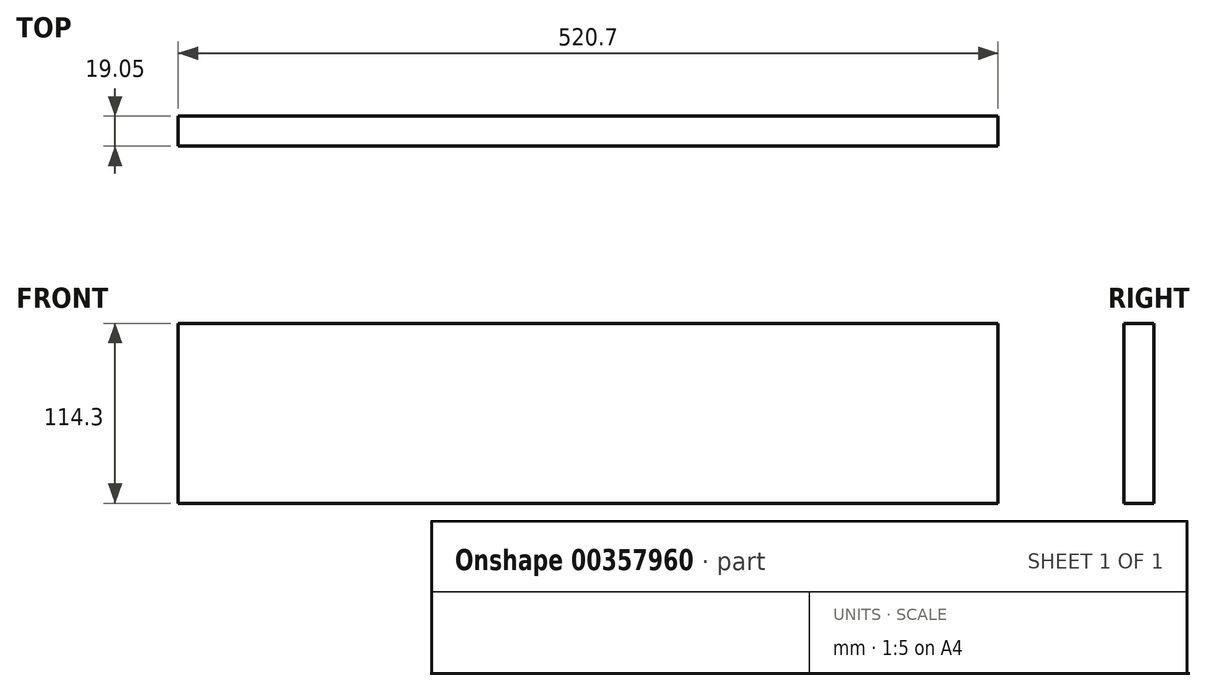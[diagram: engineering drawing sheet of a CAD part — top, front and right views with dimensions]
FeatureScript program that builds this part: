
annotation { "Feature Type Name" : "Feature", "Feature Type Description" : "" }
export const myFeature = defineFeature(function(context is Context, id is Id, definition is map)
    precondition{}
    {
        {
            var Q0;
            Q0=qCreatedBy(makeId("Front.planeOp"),FACE);
            var sketch = newSketch(context, id + "F0", { "sketchPlane" : qUnion([Q0])});
            skLineSegment(sketch, "E0.bottom", {"start": v(260.35, -57.15) * mm, "end": v(-260.35, -57.15) * mm});
            skLineSegment(sketch, "E0.top", {"start": v(260.35, 57.15) * mm, "end": v(-260.35, 57.15) * mm});
            skLineSegment(sketch, "E0.left", {"start": v(260.35, -57.15) * mm, "end": v(260.35, 57.15) * mm});
            skLineSegment(sketch, "E0.right", {"start": v(-260.35, -57.15) * mm, "end": v(-260.35, 57.15) * mm});
            skPoint(sketch, "E0.middle", {"position": v(0, 0) * mm});
            skSolve(sketch);
        }
        {
            var Q0;
            Q0=makeQuery(id+"F0.imprint","IMPRINT",FACE,{"disambiguationData":[TD([[makeQuery(id+"F0.imprint","IMPRINT",EDGE,{"derivedFrom":sQuery(id+"F0.wireOp",EDGE,"E0.bottom")}),-1.0]])]});
            extrude(context, id + "F1", {"entities" : qUnion([Q0]), "depth" : 19.05 * mm});
        }
    });
